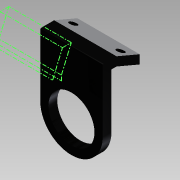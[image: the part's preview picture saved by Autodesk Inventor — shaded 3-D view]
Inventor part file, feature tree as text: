
AUTODESK INVENTOR PART (.ipt)
format: ipt  version: 2015 SP1 (Build 190203100, 203)  size: 143,872 bytes
history: native  units: mm
features: sketch x3, extrude x2, fillet x1, sweep x1
ambient origin geometry x8: Origin, YZ Plane, XZ Plane, XY Plane, X Axis, Y Axis, Z Axis, Center Point
bodies: Body1 (feature_tree)
feature tree (7):
  sketch  "Sketch1"  dims[d28=18.25mm d29=24.75mm d30=24.75mm]
  extrude  "Extrusion5"  Depth=24.75mm
  fillet  "Fillet1"  Radius=24.75mm
  sweep  "Sweep1"
  extrude  "Extrusion7"  TaperAngle=0.0deg  [1 undecoded]
  sketch  "Sketch3"  dims[d36=3.5mm d37=0.0mm d53=0.5mm]
  sketch  "Sketch6"  dims[d54=3.5mm d57=0.0mm d58=0.0mm d67=10.0mm d68=4.014257mm d70=25.0mm d71=25.0mm d72=3.0mm d73=3.0mm d74=3.0mm d75=3.0mm d76=5.0mm d77=5.0mm d78=5.0mm d79=10.0mm d80=0.0mm]
note: 1 required parameter value undecoded (feature->parameter linkage not recoverable at this tier; creation-order binding heuristic only, values carry confidence <= 0.55)
